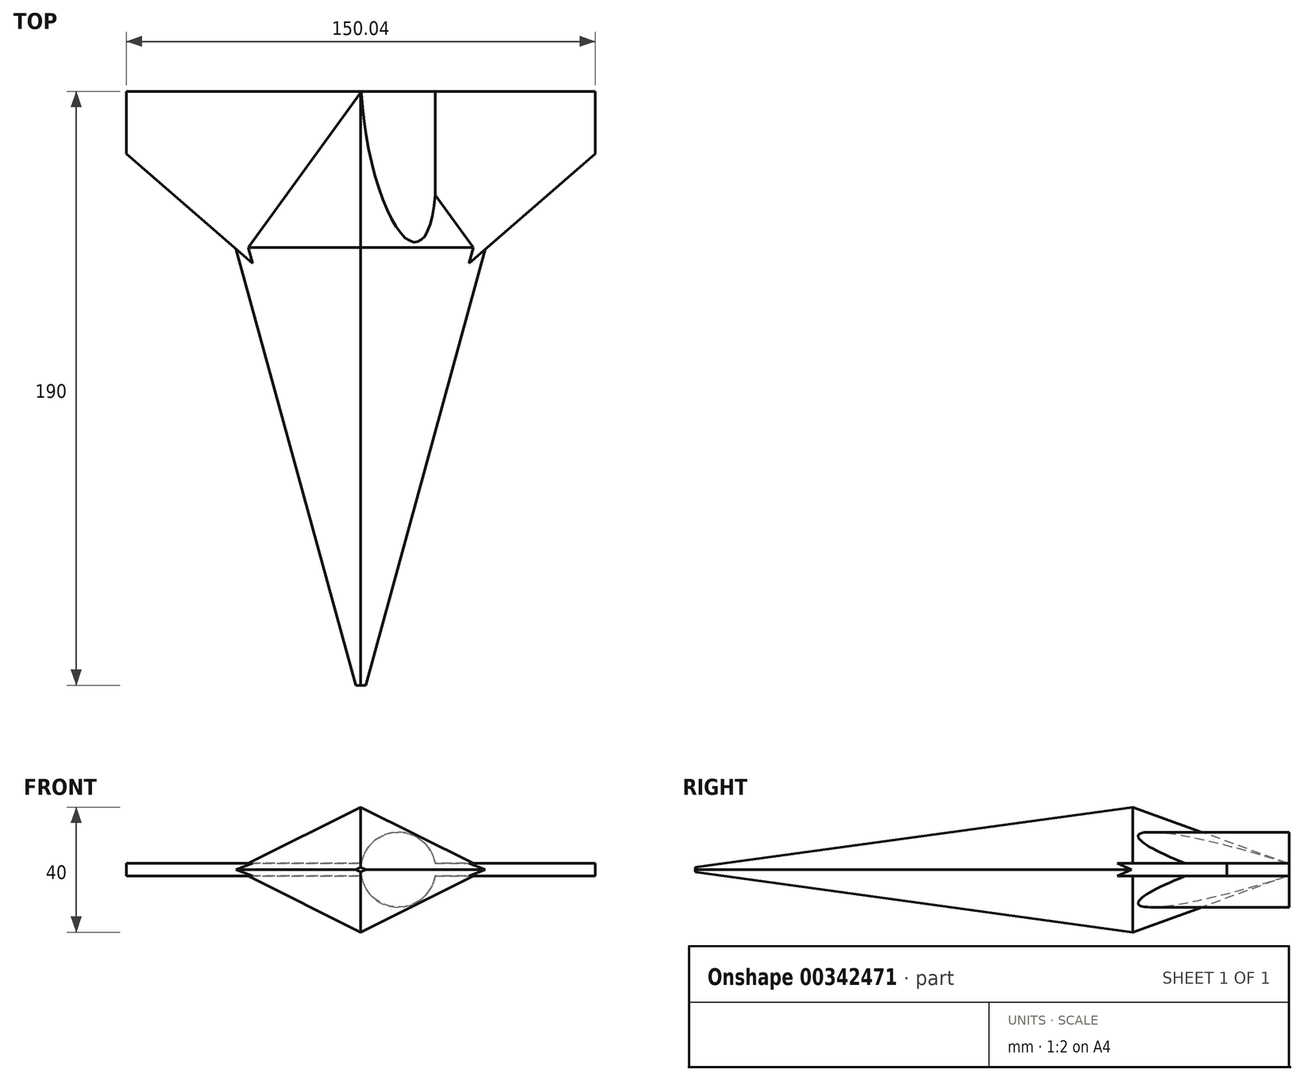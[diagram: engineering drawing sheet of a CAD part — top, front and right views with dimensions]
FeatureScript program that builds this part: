
annotation { "Feature Type Name" : "Feature", "Feature Type Description" : "" }
export const myFeature = defineFeature(function(context is Context, id is Id, definition is map)
    precondition{}
    {
        {
            var Q0;
            Q0=qCreatedBy(makeId("Front.planeOp"),FACE);
            var sketch = newSketch(context, id + "F0", { "sketchPlane" : qUnion([Q0])});
            skLineSegment(sketch, "E0", {"start": v(-40, 0) * mm, "end": v(0, 20) * mm});
            skLineSegment(sketch, "E1.MirrorCS", {"start": v(-40, 0) * mm, "end": v(0, -20) * mm});
            skLineSegment(sketch, "E2.MirrorCS", {"start": v(40, 0) * mm, "end": v(0, 20) * mm});
            skLineSegment(sketch, "E3.MirrorCS", {"start": v(40, 0) * mm, "end": v(0, -20) * mm});
            skSolve(sketch);
        }
        {
            var Q0;
            Q0=makeQuery(id+"F0.imprint","IMPRINT",FACE,{"disambiguationData":[TD([[makeQuery(id+"F0.imprint","IMPRINT",EDGE,{"derivedFrom":sQuery(id+"F0.wireOp",EDGE,"E0")}),-1.0]])]});
            extrude(context, id + "F1", {"entities" : qUnion([Q0]), "depth" : 140 * mm, "hasDraft" : true, "draftAngle" : 7 * degree, "draftPullDirection" : true, "hasSecondDirection" : true, "secondDirectionOppositeDirection" : true, "secondDirectionDepth" : 50 * mm, "hasSecondDirectionDraft" : true, "secondDirectionDraftAngle" : 18 * degree, "secondDirectionDraftPullDirection" : true});
        }
        {
            var Q0;
            Q0=qCreatedBy(makeId("Top.planeOp"),FACE);
            var sketch = newSketch(context, id + "F2", { "sketchPlane" : qUnion([Q0])});
            skLineSegment(sketch, "E4", {"start": v(0, -35) * mm, "end": v(75.02, 30) * mm});
            skLineSegment(sketch, "E5", {"start": v(75.02, 30) * mm, "end": v(75.02, 50) * mm});
            skLineSegment(sketch, "E6", {"start": v(75.02, 50) * mm, "end": v(0, 50) * mm});
            skLineSegment(sketch, "E7", {"start": v(0, 50) * mm, "end": v(0, -35) * mm});
            skLineSegment(sketch, "E8.MirrorCS", {"start": v(0, -35) * mm, "end": v(-75.02, 30) * mm});
            skLineSegment(sketch, "E9.MirrorCS", {"start": v(-75.02, 50) * mm, "end": v(0, 50) * mm});
            skLineSegment(sketch, "E10.MirrorCS", {"start": v(-75.02, 30) * mm, "end": v(-75.02, 50) * mm});
            skSolve(sketch);
        }
        {
            var Q0;
            Q0=qSketchRegion(id+"F2",true);
            extrude(context, id + "F3", {"entities" : qUnion([Q0]), "operationType" : NewBodyOperationType.ADD, "endBound" : BoundingType.SYMMETRIC, "depth" : 4 * mm});
        }
        {
            var Q0;
            Q0=qCreatedBy(makeId("Front.planeOp"),FACE);
            var sketch = newSketch(context, id + "F4", { "sketchPlane" : qUnion([Q0])});
            skCircle(sketch, "E11", {"center": v(12, 0) * mm, "radius": 12 * mm});
            skCircle(sketch, "E12.MirrorC", {"center": v(-12, 0) * mm, "radius": 12 * mm});
            skSolve(sketch);
        }
        {
            var Q0;
            Q0=makeQuery(id+"F4.imprint","IMPRINT",FACE,{"disambiguationData":[TD([[makeQuery(id+"F4.imprint","IMPRINT",EDGE,{"derivedFrom":sQuery(id+"F4.wireOp",EDGE,"E11")}),1.0]])]});
            var Q1;
            Q1=makeQuery(id+"F4.imprint","IMPRINT",FACE,{"disambiguationData":[TD([[makeQuery(id+"F4.imprint","IMPRINT",EDGE,{"derivedFrom":sQuery(id+"F4.wireOp",EDGE,"E12.MirrorC")}),-1.0]])]});
            extrude(context, id + "F5", {"entities" : qUnion([Q0, Q1]), "operationType" : NewBodyOperationType.ADD, "oppositeDirection" : true, "depth" : 50 * mm});
        }
    });
